FCSTD DOCUMENT  (FreeCAD 1.0R39109 (Git))
Label: 10000-mAh
License: All rights reserved
LicenseURL: https://en.wikipedia.org/wiki/All_rights_reserved
objects: Sketcher::SketchObject×1, PartDesign::Body×1
note: 3 computed .brp shape members not serialized (recipe doc carries the construction recipe); baked Part::Feature solids carry a one-line shape summary decoded from their .brp

FEATURE [Sketcher::SketchObject] Sketch
  ArcFitTolerance = 1e-06
  AttachmentSupport = -> [XY_Plane]
  FullyConstrained = true
  MakeInternals = false
  MapMode = 5
  sketch-geometry (5):
    g0: LineSegment StartX=-36.5 StartY=-52.5 StartZ=0 EndX=36.5 EndY=-52.5 EndZ=0
    g1: LineSegment StartX=36.5 StartY=-52.5 StartZ=0 EndX=36.5 EndY=52.5 EndZ=0
    g2: LineSegment StartX=36.5 StartY=52.5 StartZ=0 EndX=-36.5 EndY=52.5 EndZ=0
    g3: LineSegment StartX=-36.5 StartY=52.5 StartZ=0 EndX=-36.5 EndY=-52.5 EndZ=0
    g4: GeomPoint [constr] X=0 Y=0 Z=0
  constraints (12):
    c: Coincident(g0,g1)
    c: Coincident(g1,g2)
    c: Coincident(g2,g3)
    c: Coincident(g3,g0)
    c: Horizontal(g0)
    c: Horizontal(g2)
    c: Vertical(g1)
    c: Vertical(g3)
    c: Symmetric(g2,g0,g4)
    c: Distance(g1,g3) = 73
    c: Distance(g0,g2) = 105
    c: Coincident(g4,g-1)
FEATURE [PartDesign::Body] Body
  AllowCompound = false
  Group = -> [Sketch]
  Origin = -> Origin
